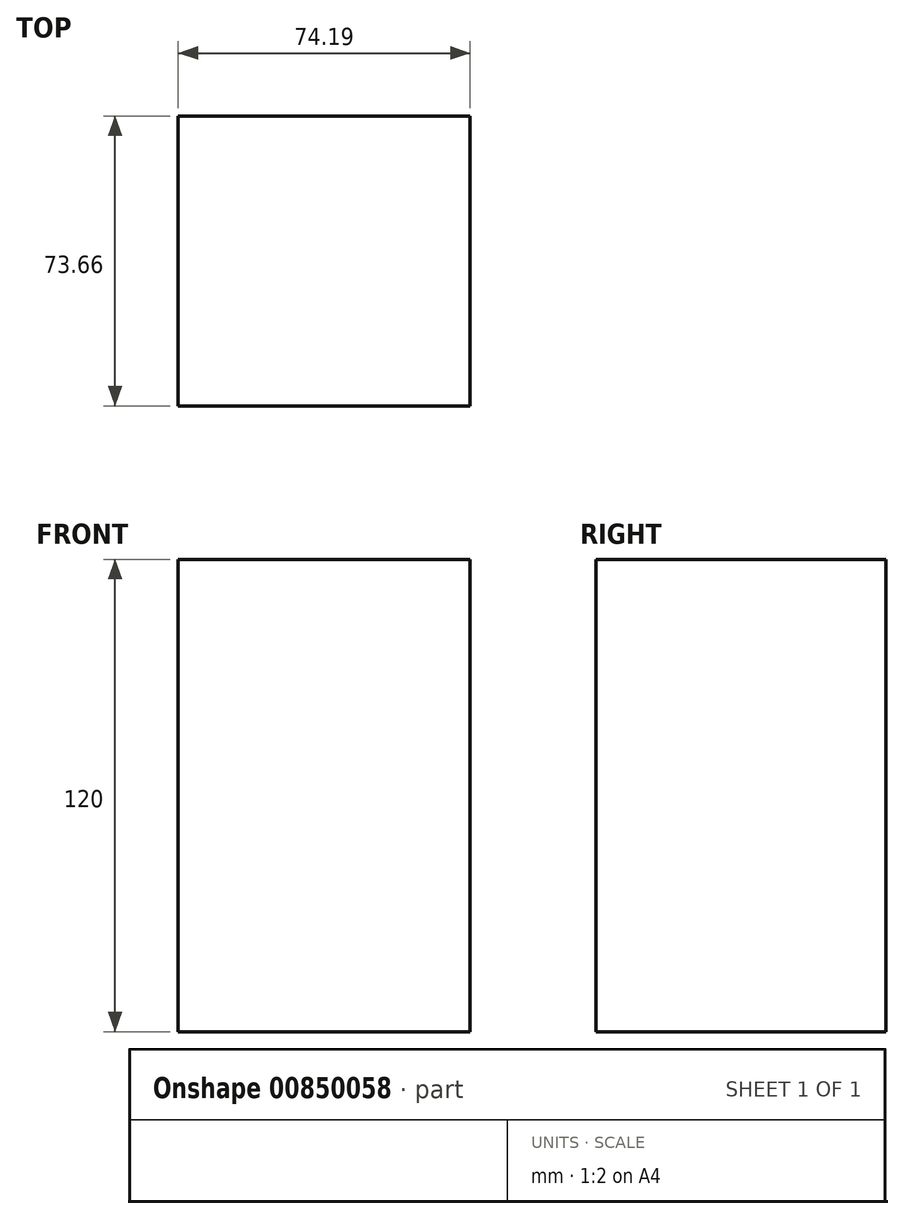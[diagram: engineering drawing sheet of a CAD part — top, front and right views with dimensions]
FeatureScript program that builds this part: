
annotation { "Feature Type Name" : "Feature", "Feature Type Description" : "" }
export const myFeature = defineFeature(function(context is Context, id is Id, definition is map)
    precondition{}
    {
        {
            var Q0;
            Q0=qCreatedBy(makeId("Top.planeOp"),FACE);
            var sketch = newSketch(context, id + "F0", { "sketchPlane" : qUnion([Q0])});
            skLineSegment(sketch, "E0.bottom", {"start": v(-45.22, 33.04) * mm, "end": v(28.97, 33.04) * mm});
            skLineSegment(sketch, "E0.top", {"start": v(-45.22, -40.62) * mm, "end": v(28.97, -40.62) * mm});
            skLineSegment(sketch, "E0.left", {"start": v(-45.22, 33.04) * mm, "end": v(-45.22, -40.62) * mm});
            skLineSegment(sketch, "E0.right", {"start": v(28.97, 33.04) * mm, "end": v(28.97, -40.62) * mm});
            skSolve(sketch);
        }
        {
            var Q0;
            Q0 = qSketchRegion(id + "F0", true);
            extrude(context, id + "F1", {"entities" : qUnion([Q0]), "depth" : 120 * mm, "offsetDistance" : 25 * mm});
        }
    });
